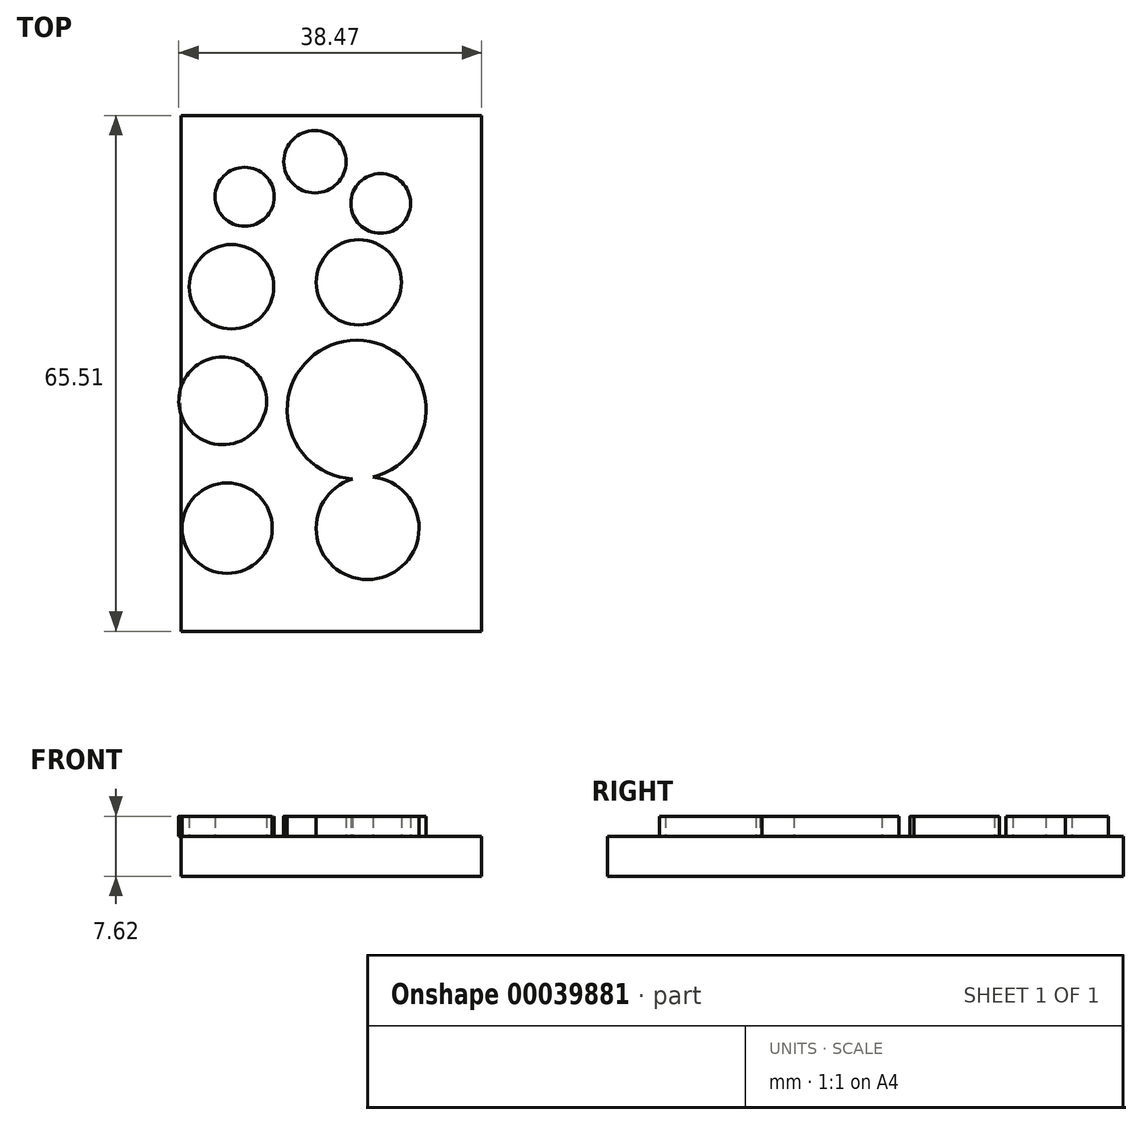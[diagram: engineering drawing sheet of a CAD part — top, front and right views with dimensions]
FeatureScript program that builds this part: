
annotation { "Feature Type Name" : "Feature", "Feature Type Description" : "" }
export const myFeature = defineFeature(function(context is Context, id is Id, definition is map)
    precondition{}
    {
        {
            var Q0;
            Q0=qCreatedBy(makeId("Top.planeOp"),FACE);
            var sketch = newSketch(context, id + "F0", { "sketchPlane" : qUnion([Q0])});
            skLineSegment(sketch, "E0.bottom", {"start": v(0, 0) * mm, "end": v(40.84, 0) * mm});
            skLineSegment(sketch, "E0.top", {"start": v(0, 66.63) * mm, "end": v(40.84, 66.63) * mm});
            skLineSegment(sketch, "E0.left", {"start": v(0, 0) * mm, "end": v(0, 66.63) * mm});
            skLineSegment(sketch, "E0.right", {"start": v(40.84, 0) * mm, "end": v(40.84, 66.63) * mm});
            skLineSegment(sketch, "E1.bottom", {"start": v(-53.94, 0) * mm, "end": v(-15.75, 0) * mm});
            skLineSegment(sketch, "E1.top", {"start": v(-53.94, 65.51) * mm, "end": v(-15.75, 65.51) * mm});
            skLineSegment(sketch, "E1.left", {"start": v(-53.94, 0) * mm, "end": v(-53.94, 65.51) * mm});
            skLineSegment(sketch, "E1.right", {"start": v(-15.75, 0) * mm, "end": v(-15.75, 65.51) * mm});
            skSolve(sketch);
        }
        {
            var Q0;
            Q0=makeQuery(id+"F0.imprint","IMPRINT",FACE,{"disambiguationData":[TD([[makeQuery(id+"F0.imprint","IMPRINT",EDGE,{"derivedFrom":sQuery(id+"F0.wireOp",EDGE,"E1.bottom")}),1.0]])]});
            extrude(context, id + "F1", {"entities" : qUnion([Q0]), "depth" : 5.08 * mm});
        }
        {
            var Q0;
            Q0=makeQuery(id+"F1.opExtrude","CAP_FACE",FACE,{"disambiguationData":[OSD([sQuery(id+"F0.wireOp",EDGE,"E1.bottom"),sQuery(id+"F0.wireOp",EDGE,"E1.top"),sQuery(id+"F0.wireOp",EDGE,"E1.left"),sQuery(id+"F0.wireOp",EDGE,"E1.right")])],"isStart":false});
            var sketch = newSketch(context, id + "F2", { "sketchPlane" : qUnion([Q0])});
            skCircle(sketch, "E2", {"center": v(-47.53, 43.77) * mm, "radius": 5.36 * mm});
            skCircle(sketch, "E3", {"center": v(-48.65, 29.27) * mm, "radius": 5.58 * mm});
            skCircle(sketch, "E4", {"center": v(-48.09, 13.1) * mm, "radius": 5.74 * mm});
            skCircle(sketch, "E5", {"center": v(-30.25, 13.1) * mm, "radius": 6.53 * mm});
            skCircle(sketch, "E6", {"center": v(-31.64, 28.16) * mm, "radius": 8.82 * mm});
            skCircle(sketch, "E7", {"center": v(-31.36, 44.33) * mm, "radius": 5.41 * mm});
            skCircle(sketch, "E8", {"center": v(-28.57, 54.36) * mm, "radius": 3.8 * mm});
            skCircle(sketch, "E9", {"center": v(-45.86, 55.2) * mm, "radius": 3.75 * mm});
            skCircle(sketch, "E10", {"center": v(-36.94, 59.66) * mm, "radius": 3.96 * mm});
            skSolve(sketch);
        }
        {
            var Q0;
            Q0 = qSketchRegion(id + "F2", true);
            extrude(context, id + "F3", {"entities" : qUnion([Q0]), "operationType" : NewBodyOperationType.ADD, "depth" : 2.54 * mm});
        }
    });
